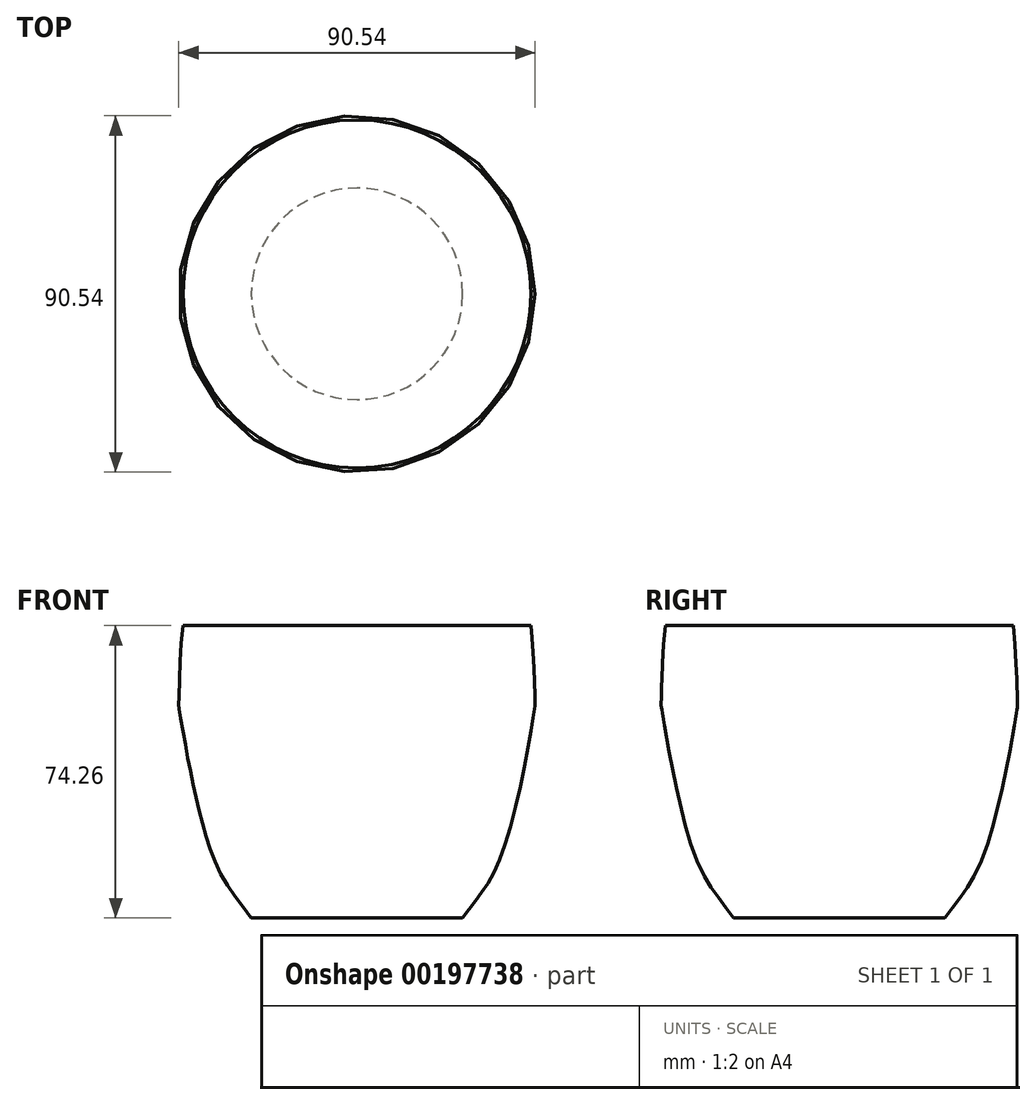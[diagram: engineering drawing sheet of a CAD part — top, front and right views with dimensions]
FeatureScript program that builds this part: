
annotation { "Feature Type Name" : "Feature", "Feature Type Description" : "" }
export const myFeature = defineFeature(function(context is Context, id is Id, definition is map)
    precondition{}
    {
        {
            var Q0;
            Q0=qCreatedBy(makeId("Front.planeOp"),FACE);
            var sketch = newSketch(context, id + "F0", { "sketchPlane" : qUnion([Q0])});
            skLineSegment(sketch, "E0", {"start": v(0, -27.6) * mm, "end": v(-26.87, -27.6) * mm});
            skFitSpline(sketch, "E1", {"points": [v(-26.87, -27.6) * mm, v(-37.46, -9.6) * mm, v(-45.27, 26.27) * mm, v(-45.27, 26.31) * mm, v(-44.2, 46.66) * mm], "startDerivative": vector(-37.2, 51.2) * mm, "endDerivative": vector(7.88, 61.39) * mm});
            skPoint(sketch, "E2", {"position": v(-42.85, 12.38) * mm});
            skLineSegment(sketch, "E3", {"start": v(-44.2, 46.66) * mm, "end": v(0, 46.66) * mm});
            skLineSegment(sketch, "E4", {"start": v(0, 46.66) * mm, "end": v(0, -27.6) * mm});
            skSolve(sketch);
        }
        {
            var Q0;
            Q0=makeQuery(id+"F0.imprint","IMPRINT",FACE,{"disambiguationData":[TD([[makeQuery(id+"F0.imprint","IMPRINT",EDGE,{"derivedFrom":sQuery(id+"F0.wireOp",EDGE,"E0")}),-1.0]])]});
            var Q1;
            Q1=sQuery(id+"F0.wireOp",EDGE,"E4");
            revolve(context, id + "F1", {"entities" : qUnion([Q0]), "axis" : qUnion([Q1]), "revolveType" : RevolveType.FULL});
        }
    });
